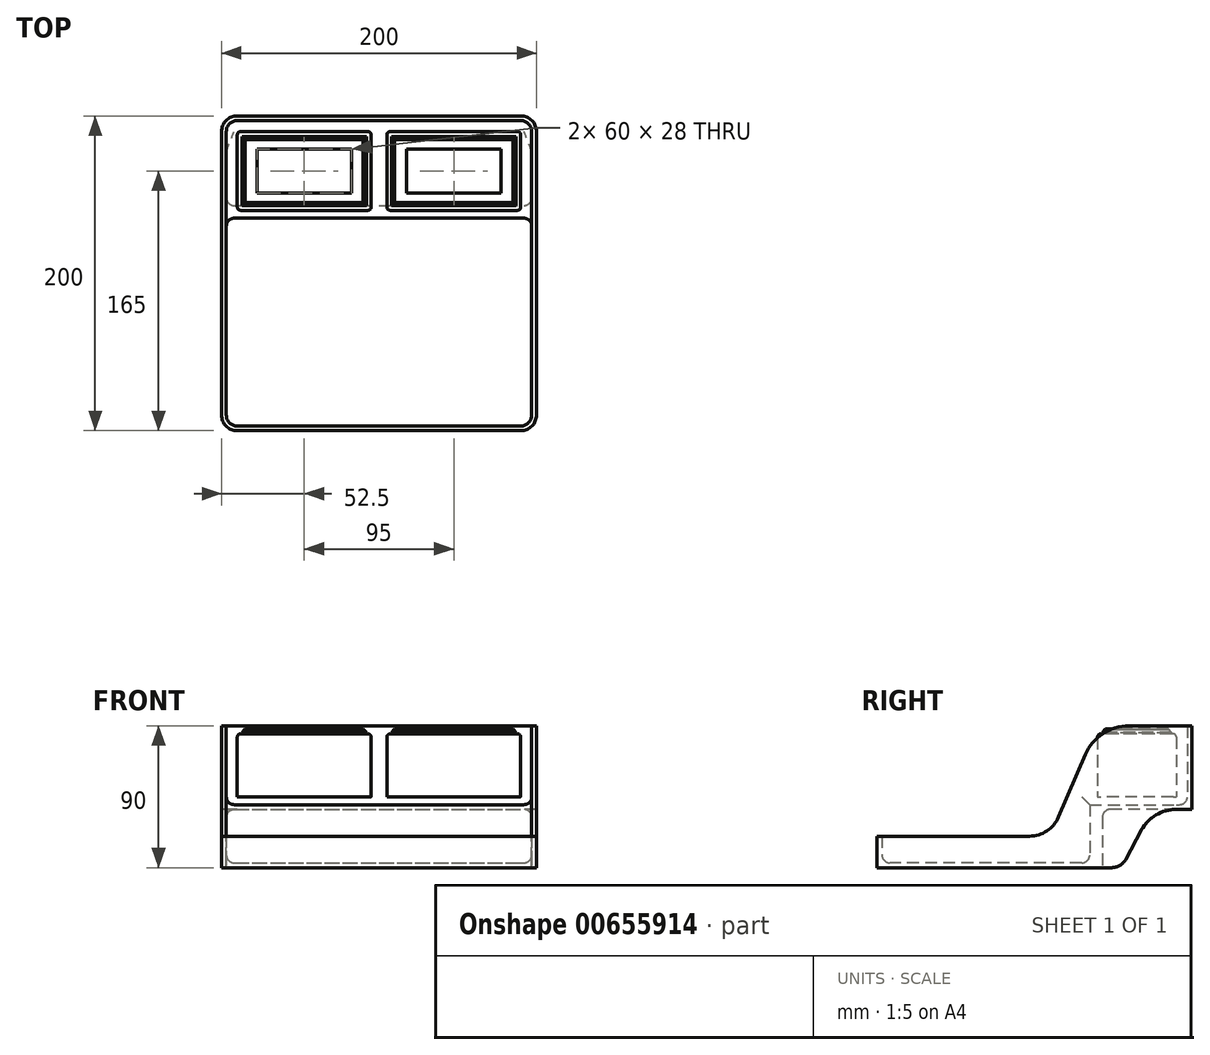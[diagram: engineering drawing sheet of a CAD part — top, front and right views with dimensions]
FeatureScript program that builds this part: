
annotation { "Feature Type Name" : "Feature", "Feature Type Description" : "" }
export const myFeature = defineFeature(function(context is Context, id is Id, definition is map)
    precondition{}
    {
        {
            var Q0;
            Q0=qCreatedBy(makeId("Top.planeOp"),FACE);
            var sketch = newSketch(context, id + "F0", { "sketchPlane" : qUnion([Q0])});
            skLineSegment(sketch, "E0.bottom", {"start": v(-90, 100) * mm, "end": v(90, 100) * mm});
            skLineSegment(sketch, "E0.top", {"start": v(-90, -100) * mm, "end": v(90, -100) * mm});
            skLineSegment(sketch, "E0.left", {"start": v(-100, 90) * mm, "end": v(-100, -90) * mm});
            skLineSegment(sketch, "E0.right", {"start": v(100, 90) * mm, "end": v(100, -90) * mm});
            skPoint(sketch, "E1.visualSharp", {"position": v(-100, 100) * mm});
            skArc(sketch, "E1.filletArc", {"start": v(-90, 100) * mm, "mid": v(-97.07, 97.07) * mm, "end": v(-100, 90) * mm});
            skPoint(sketch, "E2.visualSharp", {"position": v(100, 100) * mm});
            skArc(sketch, "E2.filletArc", {"start": v(100, 90) * mm, "mid": v(97.07, 97.07) * mm, "end": v(90, 100) * mm});
            skPoint(sketch, "E3.visualSharp", {"position": v(100, -100) * mm});
            skArc(sketch, "E3.filletArc", {"start": v(90, -100) * mm, "mid": v(97.07, -97.07) * mm, "end": v(100, -90) * mm});
            skPoint(sketch, "E4.visualSharp", {"position": v(-100, -100) * mm});
            skArc(sketch, "E4.filletArc", {"start": v(-100, -90) * mm, "mid": v(-97.07, -97.07) * mm, "end": v(-90, -100) * mm});
            skSolve(sketch);
        }
        {
            var Q0;
            Q0 = qSketchRegion(id + "F0", true);
            extrude(context, id + "F1", {"entities" : qUnion([Q0]), "depth" : 90 * mm, "offsetDistance" : 25 * mm});
        }
        {
            var Q0;
            Q0=qCreatedBy(makeId("Top.planeOp"),FACE);
            var sketch = newSketch(context, id + "F2", { "sketchPlane" : qUnion([Q0])});
            skLineSegment(sketch, "E5.bottom", {"start": v(-97, 35) * mm, "end": v(97, 35) * mm});
            skLineSegment(sketch, "E5.top", {"start": v(-90, -97) * mm, "end": v(90, -97) * mm});
            skLineSegment(sketch, "E5.left", {"start": v(-97, 35) * mm, "end": v(-97, -90) * mm});
            skLineSegment(sketch, "E5.right", {"start": v(97, 35) * mm, "end": v(97, -90) * mm});
            skPoint(sketch, "E6.visualSharp", {"position": v(97, -97) * mm});
            skArc(sketch, "E6.filletArc", {"start": v(90, -97) * mm, "mid": v(94.95, -94.95) * mm, "end": v(97, -90) * mm});
            skPoint(sketch, "E7.visualSharp", {"position": v(-97, -97) * mm});
            skArc(sketch, "E7.filletArc", {"start": v(-97, -90) * mm, "mid": v(-94.95, -94.95) * mm, "end": v(-90, -97) * mm});
            skSolve(sketch);
        }
        {
            var Q0;
            Q0 = qSketchRegion(id + "F2", true);
            extrude(context, id + "F3", {"entities" : qUnion([Q0]), "depth" : 80 * mm, "offsetDistance" : 25 * mm});
        }
        {
            var Q0;
            Q0=makeQuery(id+"F3.opExtrude","CAP_EDGE",EDGE,{"disambiguationData":[OSD([sQuery(id+"F2.wireOp",EDGE,"E5.left")])],"isStart":true});
            var Q1;
            Q1=makeQuery(id+"F3.opExtrude","CAP_EDGE",EDGE,{"disambiguationData":[OSD([sQuery(id+"F2.wireOp",EDGE,"E7.filletArc")])],"isStart":true});
            var Q2;
            Q2=makeQuery(id+"F3.opExtrude","CAP_EDGE",EDGE,{"disambiguationData":[OSD([sQuery(id+"F2.wireOp",EDGE,"E5.top")])],"isStart":true});
            var Q3;
            Q3=makeQuery(id+"F3.opExtrude","CAP_EDGE",EDGE,{"disambiguationData":[OSD([sQuery(id+"F2.wireOp",EDGE,"E6.filletArc")])],"isStart":true});
            var Q4;
            Q4=makeQuery(id+"F3.opExtrude","CAP_EDGE",EDGE,{"disambiguationData":[OSD([sQuery(id+"F2.wireOp",EDGE,"E5.right")])],"isStart":true});
            var Q5;
            Q5=makeQuery(id+"F3.opExtrude","CAP_EDGE",EDGE,{"disambiguationData":[OSD([sQuery(id+"F2.wireOp",EDGE,"E5.bottom")])],"isStart":true});
            var Q6;
            Q6=makeQuery(id+"F3.opExtrude","SWEPT_EDGE",EDGE,{"disambiguationData":[OSD([sQuery(id+"F2.wireOp",EDGE,"E5.bottom"),sQuery(id+"F2.wireOp",EDGE,"E5.left")])]});
            var Q7;
            Q7=makeQuery(id+"F3.opExtrude","SWEPT_EDGE",EDGE,{"disambiguationData":[OSD([sQuery(id+"F2.wireOp",EDGE,"E5.bottom"),sQuery(id+"F2.wireOp",EDGE,"E5.right")])]});
            fillet(context, id + "F4", {"entities" : qUnion([Q0, Q1, Q2, Q3, Q4, Q5, Q6, Q7]), "radius" : 5 * mm, "tangentPropagation" : true, "allowEdgeOverflow" : false});
        }
        {
            var Q0;
            Q0=makeQuery(id+"F3.opExtrude","SWEPT_BODY",BODY,{"disambiguationData":[OSD([sQuery(id+"F2.wireOp",EDGE,"E5.bottom"),sQuery(id+"F2.wireOp",EDGE,"E5.top"),sQuery(id+"F2.wireOp",EDGE,"E5.left"),sQuery(id+"F2.wireOp",EDGE,"E5.right"),sQuery(id+"F2.wireOp",EDGE,"E6.filletArc"),sQuery(id+"F2.wireOp",EDGE,"E7.filletArc")])]});
            var Q1;
            Q1=qCreatedBy(makeId("Top.planeOp"),FACE);
            transform(context, id + "F5", {"entities" : qUnion([Q0]), "transformType" : TransformType.TRANSLATION_DISTANCE, "transformDirection" : qUnion([Q1]), "distance" : 3 * mm, "makeCopy" : false});
        }
        {
            var Q0;
            Q0=qCreatedBy(makeId("Top.planeOp"),FACE);
            var sketch = newSketch(context, id + "F6", { "sketchPlane" : qUnion([Q0])});
            skLineSegment(sketch, "E8.bottom", {"start": v(-97, 30) * mm, "end": v(97, 30) * mm});
            skLineSegment(sketch, "E8.top", {"start": v(-90, 97) * mm, "end": v(90, 97) * mm});
            skLineSegment(sketch, "E8.left", {"start": v(-97, 30) * mm, "end": v(-97, 90) * mm});
            skLineSegment(sketch, "E8.right", {"start": v(97, 30) * mm, "end": v(97, 90) * mm});
            skPoint(sketch, "E9.visualSharp", {"position": v(-97, 97) * mm});
            skArc(sketch, "E9.filletArc", {"start": v(-90, 97) * mm, "mid": v(-94.95, 94.95) * mm, "end": v(-97, 90) * mm});
            skPoint(sketch, "E10.visualSharp", {"position": v(97, 97) * mm});
            skArc(sketch, "E10.filletArc", {"start": v(97, 90) * mm, "mid": v(94.95, 94.95) * mm, "end": v(90, 97) * mm});
            skSolve(sketch);
        }
        {
            var Q0;
            Q0 = qSketchRegion(id + "F6", true);
            extrude(context, id + "F7", {"entities" : qUnion([Q0]), "depth" : 50 * mm, "offsetDistance" : 25 * mm});
        }
        {
            var Q0;
            Q0=makeQuery(id+"F7.opExtrude","CAP_EDGE",EDGE,{"disambiguationData":[OSD([sQuery(id+"F6.wireOp",EDGE,"E8.left")])],"isStart":true});
            var Q1;
            Q1=makeQuery(id+"F7.opExtrude","CAP_EDGE",EDGE,{"disambiguationData":[OSD([sQuery(id+"F6.wireOp",EDGE,"E9.filletArc")])],"isStart":true});
            var Q2;
            Q2=makeQuery(id+"F7.opExtrude","CAP_EDGE",EDGE,{"disambiguationData":[OSD([sQuery(id+"F6.wireOp",EDGE,"E8.top")])],"isStart":true});
            var Q3;
            Q3=makeQuery(id+"F7.opExtrude","CAP_EDGE",EDGE,{"disambiguationData":[OSD([sQuery(id+"F6.wireOp",EDGE,"E10.filletArc")])],"isStart":true});
            var Q4;
            Q4=makeQuery(id+"F7.opExtrude","CAP_EDGE",EDGE,{"disambiguationData":[OSD([sQuery(id+"F6.wireOp",EDGE,"E8.right")])],"isStart":true});
            fillet(context, id + "F8", {"entities" : qUnion([Q0, Q1, Q2, Q3, Q4]), "radius" : 5 * mm, "tangentPropagation" : true, "allowEdgeOverflow" : false});
        }
        {
            var Q0;
            Q0=makeQuery(id+"F7.opExtrude","SWEPT_BODY",BODY,{"disambiguationData":[OSD([sQuery(id+"F6.wireOp",EDGE,"E8.bottom"),sQuery(id+"F6.wireOp",EDGE,"E8.top"),sQuery(id+"F6.wireOp",EDGE,"E8.left"),sQuery(id+"F6.wireOp",EDGE,"E8.right"),sQuery(id+"F6.wireOp",EDGE,"E9.filletArc"),sQuery(id+"F6.wireOp",EDGE,"E10.filletArc")])]});
            var Q1;
            Q1=qCreatedBy(makeId("Top.planeOp"),FACE);
            transform(context, id + "F9", {"entities" : qUnion([Q0]), "transformType" : TransformType.TRANSLATION_DISTANCE, "transformDirection" : qUnion([Q1]), "distance" : 40 * mm, "makeCopy" : false});
        }
        {
            var Q0;
            Q0=makeQuery(id+"F7.opExtrude","SWEPT_BODY",BODY,{"disambiguationData":[OSD([sQuery(id+"F6.wireOp",EDGE,"E8.bottom"),sQuery(id+"F6.wireOp",EDGE,"E8.top"),sQuery(id+"F6.wireOp",EDGE,"E8.left"),sQuery(id+"F6.wireOp",EDGE,"E8.right"),sQuery(id+"F6.wireOp",EDGE,"E9.filletArc"),sQuery(id+"F6.wireOp",EDGE,"E10.filletArc")])]});
            var Q1;
            Q1=makeQuery(id+"F3.opExtrude","SWEPT_BODY",BODY,{"disambiguationData":[OSD([sQuery(id+"F2.wireOp",EDGE,"E5.bottom"),sQuery(id+"F2.wireOp",EDGE,"E5.top"),sQuery(id+"F2.wireOp",EDGE,"E5.left"),sQuery(id+"F2.wireOp",EDGE,"E5.right"),sQuery(id+"F2.wireOp",EDGE,"E6.filletArc"),sQuery(id+"F2.wireOp",EDGE,"E7.filletArc")])]});
            var Q2;
            Q2=makeQuery(id+"F1.opExtrude","SWEPT_BODY",BODY,{"disambiguationData":[OSD([sQuery(id+"F0.wireOp",EDGE,"E0.bottom"),sQuery(id+"F0.wireOp",EDGE,"E0.top"),sQuery(id+"F0.wireOp",EDGE,"E0.left"),sQuery(id+"F0.wireOp",EDGE,"E0.right"),sQuery(id+"F0.wireOp",EDGE,"E1.filletArc"),sQuery(id+"F0.wireOp",EDGE,"E2.filletArc"),sQuery(id+"F0.wireOp",EDGE,"E3.filletArc"),sQuery(id+"F0.wireOp",EDGE,"E4.filletArc")])]});
            booleanBodies(context, id + "F10", {"operationType" : BooleanOperationType.SUBTRACTION, "tools" : qUnion([Q0, Q1]), "targets" : qUnion([Q2])});
        }
        {
            var Q0;
            Q0=qCreatedBy(makeId("Top.planeOp"),FACE);
            var sketch = newSketch(context, id + "F11", { "sketchPlane" : qUnion([Q0])});
            skLineSegment(sketch, "E11.bottom", {"start": v(-97, 105) * mm, "end": v(97, 105) * mm});
            skLineSegment(sketch, "E11.top", {"start": v(-92, 43) * mm, "end": v(92, 43) * mm});
            skLineSegment(sketch, "E11.left", {"start": v(-97, 105) * mm, "end": v(-97, 48) * mm});
            skLineSegment(sketch, "E11.right", {"start": v(97, 105) * mm, "end": v(97, 48) * mm});
            skPoint(sketch, "E12.visualSharp", {"position": v(-97, 43) * mm});
            skArc(sketch, "E12.filletArc", {"start": v(-97, 48) * mm, "mid": v(-95.54, 44.46) * mm, "end": v(-92, 43) * mm});
            skPoint(sketch, "E13.visualSharp", {"position": v(97, 43) * mm});
            skArc(sketch, "E13.filletArc", {"start": v(92, 43) * mm, "mid": v(95.54, 44.46) * mm, "end": v(97, 48) * mm});
            skSolve(sketch);
        }
        {
            var Q0;
            Q0=makeQuery(id+"F11.imprint","IMPRINT",FACE,{"disambiguationData":[TD([[makeQuery(id+"F11.imprint","IMPRINT",EDGE,{"derivedFrom":sQuery(id+"F11.wireOp",EDGE,"E11.bottom")}),-1.0]])]});
            extrude(context, id + "F12", {"entities" : qUnion([Q0]), "depth" : 37 * mm, "offsetDistance" : 25 * mm});
        }
        {
            var Q0;
            Q0=makeQuery(id+"F12.opExtrude","CAP_EDGE",EDGE,{"disambiguationData":[OSD([sQuery(id+"F11.wireOp",EDGE,"E11.top")])],"isStart":false});
            var Q1;
            Q1=makeQuery(id+"F12.opExtrude","CAP_EDGE",EDGE,{"disambiguationData":[OSD([sQuery(id+"F11.wireOp",EDGE,"E13.filletArc")])],"isStart":false});
            var Q2;
            Q2=makeQuery(id+"F12.opExtrude","CAP_EDGE",EDGE,{"disambiguationData":[OSD([sQuery(id+"F11.wireOp",EDGE,"E11.right")])],"isStart":false});
            var Q3;
            Q3=makeQuery(id+"F12.opExtrude","CAP_EDGE",EDGE,{"disambiguationData":[OSD([sQuery(id+"F11.wireOp",EDGE,"E12.filletArc")])],"isStart":false});
            var Q4;
            Q4=makeQuery(id+"F12.opExtrude","CAP_EDGE",EDGE,{"disambiguationData":[OSD([sQuery(id+"F11.wireOp",EDGE,"E11.left")])],"isStart":false});
            fillet(context, id + "F13", {"entities" : qUnion([Q0, Q1, Q2, Q3, Q4]), "radius" : 5 * mm, "tangentPropagation" : true, "allowEdgeOverflow" : false});
        }
        {
            var Q0;
            Q0=makeQuery(id+"F12.opExtrude","SWEPT_BODY",BODY,{"disambiguationData":[OSD([sQuery(id+"F11.wireOp",EDGE,"E11.bottom"),sQuery(id+"F11.wireOp",EDGE,"E11.top"),sQuery(id+"F11.wireOp",EDGE,"E11.left"),sQuery(id+"F11.wireOp",EDGE,"E11.right"),sQuery(id+"F11.wireOp",EDGE,"E12.filletArc"),sQuery(id+"F11.wireOp",EDGE,"E13.filletArc")])]});
            var Q1;
            Q1=makeQuery(id+"F1.opExtrude","SWEPT_BODY",BODY,{"disambiguationData":[OSD([sQuery(id+"F0.wireOp",EDGE,"E0.bottom"),sQuery(id+"F0.wireOp",EDGE,"E0.top"),sQuery(id+"F0.wireOp",EDGE,"E0.left"),sQuery(id+"F0.wireOp",EDGE,"E0.right"),sQuery(id+"F0.wireOp",EDGE,"E1.filletArc"),sQuery(id+"F0.wireOp",EDGE,"E2.filletArc"),sQuery(id+"F0.wireOp",EDGE,"E3.filletArc"),sQuery(id+"F0.wireOp",EDGE,"E4.filletArc")])]});
            booleanBodies(context, id + "F14", {"operationType" : BooleanOperationType.SUBTRACTION, "tools" : qUnion([Q0]), "targets" : qUnion([Q1])});
        }
        {
            var Q0;
            Q0=qCreatedBy(makeId("Right.planeOp"),FACE);
            var sketch = newSketch(context, id + "F15", { "sketchPlane" : qUnion([Q0])});
            skLineSegment(sketch, "E14", {"start": v(105, 37) * mm, "end": v(89.9, 37) * mm});
            skLineSegment(sketch, "E15", {"start": v(67.91, 23.89) * mm, "end": v(57.84, 5.24) * mm});
            skLineSegment(sketch, "E16", {"start": v(49.04, 0) * mm, "end": v(25.08, 0) * mm});
            skLineSegment(sketch, "E17", {"start": v(25.08, 0) * mm, "end": v(25.08, -10) * mm});
            skLineSegment(sketch, "E18", {"start": v(25.08, -10) * mm, "end": v(105, -10) * mm});
            skLineSegment(sketch, "E19", {"start": v(105, -10) * mm, "end": v(105, 37) * mm});
            skPoint(sketch, "E20.visualSharp", {"position": v(75, 37) * mm});
            skArc(sketch, "E20.filletArc", {"start": v(89.9, 37) * mm, "mid": v(77.1, 33.47) * mm, "end": v(67.91, 23.89) * mm});
            skPoint(sketch, "E21.visualSharp", {"position": v(55, 0) * mm});
            skArc(sketch, "E21.filletArc", {"start": v(49.04, 0) * mm, "mid": v(54.16, 1.41) * mm, "end": v(57.84, 5.24) * mm});
            skSolve(sketch);
        }
        {
            var Q0;
            Q0=makeQuery(id+"F15.imprint","IMPRINT",FACE,{"disambiguationData":[TD([[makeQuery(id+"F15.imprint","IMPRINT",EDGE,{"derivedFrom":sQuery(id+"F15.wireOp",EDGE,"E14")}),1.0]])]});
            extrude(context, id + "F16", {"entities" : qUnion([Q0]), "endBound" : BoundingType.SYMMETRIC, "depth" : 210 * mm, "offsetDistance" : 25 * mm});
        }
        {
            var Q0;
            Q0=qCreatedBy(makeId("Right.planeOp"),FACE);
            var sketch = newSketch(context, id + "F17", { "sketchPlane" : qUnion([Q0])});
            skLineSegment(sketch, "E22", {"start": v(-105, 20) * mm, "end": v(-3.19, 20) * mm});
            skLineSegment(sketch, "E23", {"start": v(15.2, 32.12) * mm, "end": v(32.2, 71.82) * mm});
            skLineSegment(sketch, "E24", {"start": v(59.78, 90) * mm, "end": v(80, 90) * mm});
            skLineSegment(sketch, "E25", {"start": v(80, 90) * mm, "end": v(80, 100) * mm});
            skLineSegment(sketch, "E26", {"start": v(80, 100) * mm, "end": v(-105, 100) * mm});
            skLineSegment(sketch, "E27", {"start": v(-105, 100) * mm, "end": v(-105, 20) * mm});
            skPoint(sketch, "E28.visualSharp", {"position": v(40, 90) * mm});
            skArc(sketch, "E28.filletArc", {"start": v(59.78, 90) * mm, "mid": v(43.27, 85.05) * mm, "end": v(32.2, 71.82) * mm});
            skPoint(sketch, "E29.visualSharp", {"position": v(10, 20) * mm});
            skArc(sketch, "E29.filletArc", {"start": v(-3.19, 20) * mm, "mid": v(7.82, 23.3) * mm, "end": v(15.2, 32.12) * mm});
            skSolve(sketch);
        }
        {
            var Q0;
            Q0=makeQuery(id+"F17.imprint","IMPRINT",FACE,{"disambiguationData":[TD([[makeQuery(id+"F17.imprint","IMPRINT",EDGE,{"derivedFrom":sQuery(id+"F17.wireOp",EDGE,"E22")}),1.0]])]});
            extrude(context, id + "F18", {"entities" : qUnion([Q0]), "endBound" : BoundingType.SYMMETRIC, "depth" : 210 * mm, "offsetDistance" : 25 * mm});
        }
        {
            var Q0;
            Q0=makeQuery(id+"F16.opExtrude","SWEPT_BODY",BODY,{"disambiguationData":[OSD([sQuery(id+"F15.wireOp",EDGE,"E14"),sQuery(id+"F15.wireOp",EDGE,"E15"),sQuery(id+"F15.wireOp",EDGE,"E16"),sQuery(id+"F15.wireOp",EDGE,"E17"),sQuery(id+"F15.wireOp",EDGE,"E18"),sQuery(id+"F15.wireOp",EDGE,"E19"),sQuery(id+"F15.wireOp",EDGE,"E20.filletArc"),sQuery(id+"F15.wireOp",EDGE,"E21.filletArc")])]});
            var Q1;
            Q1=makeQuery(id+"F18.opExtrude","SWEPT_BODY",BODY,{"disambiguationData":[OSD([sQuery(id+"F17.wireOp",EDGE,"E22"),sQuery(id+"F17.wireOp",EDGE,"E23"),sQuery(id+"F17.wireOp",EDGE,"E24"),sQuery(id+"F17.wireOp",EDGE,"E25"),sQuery(id+"F17.wireOp",EDGE,"E26"),sQuery(id+"F17.wireOp",EDGE,"E27"),sQuery(id+"F17.wireOp",EDGE,"E28.filletArc"),sQuery(id+"F17.wireOp",EDGE,"E29.filletArc")])]});
            var Q2;
            Q2=makeQuery(id+"F1.opExtrude","SWEPT_BODY",BODY,{"disambiguationData":[OSD([sQuery(id+"F0.wireOp",EDGE,"E0.bottom"),sQuery(id+"F0.wireOp",EDGE,"E0.top"),sQuery(id+"F0.wireOp",EDGE,"E0.left"),sQuery(id+"F0.wireOp",EDGE,"E0.right"),sQuery(id+"F0.wireOp",EDGE,"E1.filletArc"),sQuery(id+"F0.wireOp",EDGE,"E2.filletArc"),sQuery(id+"F0.wireOp",EDGE,"E3.filletArc"),sQuery(id+"F0.wireOp",EDGE,"E4.filletArc")])]});
            booleanBodies(context, id + "F19", {"operationType" : BooleanOperationType.SUBTRACTION, "tools" : qUnion([Q0, Q1]), "targets" : qUnion([Q2])});
        }
        {
            var Q0;
            Q0=qCreatedBy(makeId("Top.planeOp"),FACE);
            var sketch = newSketch(context, id + "F20", { "sketchPlane" : qUnion([Q0])});
            skLineSegment(sketch, "E30.bottom", {"start": v(5, 90) * mm, "end": v(90, 90) * mm});
            skLineSegment(sketch, "E30.top", {"start": v(5, 40) * mm, "end": v(90, 40) * mm});
            skLineSegment(sketch, "E30.left", {"start": v(5, 90) * mm, "end": v(5, 40) * mm});
            skLineSegment(sketch, "E30.right", {"start": v(90, 90) * mm, "end": v(90, 40) * mm});
            skLineSegment(sketch, "E31.bottom", {"start": v(-5, 90) * mm, "end": v(-90, 90) * mm});
            skLineSegment(sketch, "E31.top", {"start": v(-5, 40) * mm, "end": v(-90, 40) * mm});
            skLineSegment(sketch, "E31.left", {"start": v(-5, 90) * mm, "end": v(-5, 40) * mm});
            skLineSegment(sketch, "E31.right", {"start": v(-90, 90) * mm, "end": v(-90, 40) * mm});
            skSolve(sketch);
        }
        {
            var Q0;
            Q0=makeQuery(id+"F20.imprint","IMPRINT",FACE,{"disambiguationData":[TD([[makeQuery(id+"F20.imprint","IMPRINT",EDGE,{"derivedFrom":sQuery(id+"F20.wireOp",EDGE,"E31.bottom")}),1.0]])]});
            var Q1;
            Q1=makeQuery(id+"F20.imprint","IMPRINT",FACE,{"disambiguationData":[TD([[makeQuery(id+"F20.imprint","IMPRINT",EDGE,{"derivedFrom":sQuery(id+"F20.wireOp",EDGE,"E30.bottom")}),-1.0]])]});
            extrude(context, id + "F21", {"entities" : qUnion([Q0, Q1]), "depth" : 40 * mm, "offsetDistance" : 25 * mm});
        }
        {
            var Q0;
            Q0=makeQuery(id+"F21.opExtrude","SWEPT_EDGE",EDGE,{"disambiguationData":[OSD([sQuery(id+"F20.wireOp",EDGE,"E31.top"),sQuery(id+"F20.wireOp",EDGE,"E31.right")])]});
            var Q1;
            Q1=makeQuery(id+"F21.opExtrude","SWEPT_EDGE",EDGE,{"disambiguationData":[OSD([sQuery(id+"F20.wireOp",EDGE,"E31.top"),sQuery(id+"F20.wireOp",EDGE,"E31.left")])]});
            var Q2;
            Q2=makeQuery(id+"F21.opExtrude","SWEPT_EDGE",EDGE,{"disambiguationData":[OSD([sQuery(id+"F20.wireOp",EDGE,"E30.top"),sQuery(id+"F20.wireOp",EDGE,"E30.left")])]});
            var Q3;
            Q3=makeQuery(id+"F21.opExtrude","SWEPT_EDGE",EDGE,{"disambiguationData":[OSD([sQuery(id+"F20.wireOp",EDGE,"E30.top"),sQuery(id+"F20.wireOp",EDGE,"E30.right")])]});
            var Q4;
            Q4=makeQuery(id+"F21.opExtrude","SWEPT_EDGE",EDGE,{"disambiguationData":[OSD([sQuery(id+"F20.wireOp",EDGE,"E31.bottom"),sQuery(id+"F20.wireOp",EDGE,"E31.right")])]});
            var Q5;
            Q5=makeQuery(id+"F21.opExtrude","SWEPT_EDGE",EDGE,{"disambiguationData":[OSD([sQuery(id+"F20.wireOp",EDGE,"E31.bottom"),sQuery(id+"F20.wireOp",EDGE,"E31.left")])]});
            var Q6;
            Q6=makeQuery(id+"F21.opExtrude","SWEPT_EDGE",EDGE,{"disambiguationData":[OSD([sQuery(id+"F20.wireOp",EDGE,"E30.bottom"),sQuery(id+"F20.wireOp",EDGE,"E30.left")])]});
            var Q7;
            Q7=makeQuery(id+"F21.opExtrude","SWEPT_EDGE",EDGE,{"disambiguationData":[OSD([sQuery(id+"F20.wireOp",EDGE,"E30.bottom"),sQuery(id+"F20.wireOp",EDGE,"E30.right")])]});
            var Q8;
            Q8=makeQuery(id+"F21.opExtrude","CAP_EDGE",EDGE,{"disambiguationData":[OSD([sQuery(id+"F20.wireOp",EDGE,"E31.bottom")])],"isStart":false});
            var Q9;
            Q9=makeQuery(id+"F21.opExtrude","CAP_EDGE",EDGE,{"disambiguationData":[OSD([sQuery(id+"F20.wireOp",EDGE,"E31.right")])],"isStart":false});
            var Q10;
            Q10=makeQuery(id+"F21.opExtrude","CAP_EDGE",EDGE,{"disambiguationData":[OSD([sQuery(id+"F20.wireOp",EDGE,"E31.left")])],"isStart":false});
            var Q11;
            Q11=makeQuery(id+"F21.opExtrude","CAP_EDGE",EDGE,{"disambiguationData":[OSD([sQuery(id+"F20.wireOp",EDGE,"E30.left")])],"isStart":false});
            var Q12;
            Q12=makeQuery(id+"F21.opExtrude","CAP_EDGE",EDGE,{"disambiguationData":[OSD([sQuery(id+"F20.wireOp",EDGE,"E30.right")])],"isStart":false});
            var Q13;
            Q13=makeQuery(id+"F21.opExtrude","CAP_EDGE",EDGE,{"disambiguationData":[OSD([sQuery(id+"F20.wireOp",EDGE,"E30.top")])],"isStart":false});
            var Q14;
            Q14=makeQuery(id+"F21.opExtrude","CAP_EDGE",EDGE,{"disambiguationData":[OSD([sQuery(id+"F20.wireOp",EDGE,"E30.bottom")])],"isStart":false});
            var Q15;
            Q15=makeQuery(id+"F21.opExtrude","CAP_EDGE",EDGE,{"disambiguationData":[OSD([sQuery(id+"F20.wireOp",EDGE,"E31.top")])],"isStart":false});
            fillet(context, id + "F22", {"entities" : qUnion([Q0, Q1, Q2, Q3, Q4, Q5, Q6, Q7, Q8, Q9, Q10, Q11, Q12, Q13, Q14, Q15]), "radius" : 2 * mm, "tangentPropagation" : true, "allowEdgeOverflow" : false});
        }
        {
            var Q0;
            Q0=makeQuery(id+"F21.opExtrude","SWEPT_BODY",BODY,{"disambiguationData":[OSD([sQuery(id+"F20.wireOp",EDGE,"E31.bottom"),sQuery(id+"F20.wireOp",EDGE,"E31.top"),sQuery(id+"F20.wireOp",EDGE,"E31.left"),sQuery(id+"F20.wireOp",EDGE,"E31.right")])]});
            var Q1;
            Q1=makeQuery(id+"F21.opExtrude","SWEPT_BODY",BODY,{"disambiguationData":[OSD([sQuery(id+"F20.wireOp",EDGE,"E30.bottom"),sQuery(id+"F20.wireOp",EDGE,"E30.top"),sQuery(id+"F20.wireOp",EDGE,"E30.left"),sQuery(id+"F20.wireOp",EDGE,"E30.right")])]});
            var Q2;
            Q2=qCreatedBy(makeId("Top.planeOp"),FACE);
            transform(context, id + "F23", {"entities" : qUnion([Q0, Q1]), "transformType" : TransformType.TRANSLATION_DISTANCE, "transformDirection" : qUnion([Q2]), "distance" : 45 * mm, "makeCopy" : false});
        }
        {
            var Q0;
            Q0=qCreatedBy(makeId("Top.planeOp"),FACE);
            var sketch = newSketch(context, id + "F24", { "sketchPlane" : qUnion([Q0])});
            skLineSegment(sketch, "E32.bottom", {"start": v(8, 87) * mm, "end": v(87, 87) * mm});
            skLineSegment(sketch, "E32.top", {"start": v(8, 43) * mm, "end": v(87, 43) * mm});
            skLineSegment(sketch, "E32.left", {"start": v(8, 87) * mm, "end": v(8, 43) * mm});
            skLineSegment(sketch, "E32.right", {"start": v(87, 87) * mm, "end": v(87, 43) * mm});
            skLineSegment(sketch, "E33.bottom", {"start": v(-87, 87) * mm, "end": v(-8, 87) * mm});
            skLineSegment(sketch, "E33.top", {"start": v(-87, 43) * mm, "end": v(-8, 43) * mm});
            skLineSegment(sketch, "E33.left", {"start": v(-87, 87) * mm, "end": v(-87, 43) * mm});
            skLineSegment(sketch, "E33.right", {"start": v(-8, 87) * mm, "end": v(-8, 43) * mm});
            skSolve(sketch);
        }
        {
            var Q0;
            Q0 = qSketchRegion(id + "F24", true);
            extrude(context, id + "F25", {"entities" : qUnion([Q0]), "depth" : 3 * mm, "offsetDistance" : 25 * mm});
        }
        {
            var Q0;
            Q0=makeQuery(id+"F25.opExtrude","CAP_EDGE",EDGE,{"disambiguationData":[OSD([sQuery(id+"F24.wireOp",EDGE,"E33.left")])],"isStart":false});
            var Q1;
            Q1=makeQuery(id+"F25.opExtrude","CAP_EDGE",EDGE,{"disambiguationData":[OSD([sQuery(id+"F24.wireOp",EDGE,"E33.top")])],"isStart":false});
            var Q2;
            Q2=makeQuery(id+"F25.opExtrude","CAP_EDGE",EDGE,{"disambiguationData":[OSD([sQuery(id+"F24.wireOp",EDGE,"E33.right")])],"isStart":false});
            var Q3;
            Q3=makeQuery(id+"F25.opExtrude","CAP_EDGE",EDGE,{"disambiguationData":[OSD([sQuery(id+"F24.wireOp",EDGE,"E33.bottom")])],"isStart":false});
            var Q4;
            Q4=makeQuery(id+"F25.opExtrude","CAP_EDGE",EDGE,{"disambiguationData":[OSD([sQuery(id+"F24.wireOp",EDGE,"E32.left")])],"isStart":false});
            var Q5;
            Q5=makeQuery(id+"F25.opExtrude","CAP_EDGE",EDGE,{"disambiguationData":[OSD([sQuery(id+"F24.wireOp",EDGE,"E32.bottom")])],"isStart":false});
            var Q6;
            Q6=makeQuery(id+"F25.opExtrude","CAP_EDGE",EDGE,{"disambiguationData":[OSD([sQuery(id+"F24.wireOp",EDGE,"E32.top")])],"isStart":false});
            var Q7;
            Q7=makeQuery(id+"F25.opExtrude","CAP_EDGE",EDGE,{"disambiguationData":[OSD([sQuery(id+"F24.wireOp",EDGE,"E32.right")])],"isStart":false});
            chamfer(context, id + "F26", {"entities" : qUnion([Q0, Q1, Q2, Q3, Q4, Q5, Q6, Q7]), "width" : 2 * mm, "tangentPropagation" : true});
        }
        {
            var Q0;
            Q0=makeQuery(id+"F25.opExtrude","SWEPT_BODY",BODY,{"disambiguationData":[OSD([sQuery(id+"F24.wireOp",EDGE,"E33.bottom"),sQuery(id+"F24.wireOp",EDGE,"E33.top"),sQuery(id+"F24.wireOp",EDGE,"E33.left"),sQuery(id+"F24.wireOp",EDGE,"E33.right")])]});
            var Q1;
            Q1=makeQuery(id+"F25.opExtrude","SWEPT_BODY",BODY,{"disambiguationData":[OSD([sQuery(id+"F24.wireOp",EDGE,"E32.bottom"),sQuery(id+"F24.wireOp",EDGE,"E32.top"),sQuery(id+"F24.wireOp",EDGE,"E32.left"),sQuery(id+"F24.wireOp",EDGE,"E32.right")])]});
            var Q2;
            Q2=qCreatedBy(makeId("Top.planeOp"),FACE);
            transform(context, id + "F27", {"entities" : qUnion([Q0, Q1]), "transformType" : TransformType.TRANSLATION_DISTANCE, "transformDirection" : qUnion([Q2]), "distance" : 85 * mm, "makeCopy" : false});
        }
        {
            var Q0;
            Q0=makeQuery(id+"F24.imprint","IMPRINT",FACE,{"disambiguationData":[TD([[makeQuery(id+"F24.imprint","IMPRINT",EDGE,{"derivedFrom":sQuery(id+"F24.wireOp",EDGE,"E33.bottom")}),-1.0]])]});
            var sketch = newSketch(context, id + "F28", { "sketchPlane" : qUnion([Q0])});
            skLineSegment(sketch, "E34.bottom", {"start": v(10, 85) * mm, "end": v(85, 85) * mm});
            skLineSegment(sketch, "E34.top", {"start": v(10, 45) * mm, "end": v(85, 45) * mm});
            skLineSegment(sketch, "E34.left", {"start": v(10, 85) * mm, "end": v(10, 45) * mm});
            skLineSegment(sketch, "E34.right", {"start": v(85, 85) * mm, "end": v(85, 45) * mm});
            skLineSegment(sketch, "E35.bottom", {"start": v(-85, 85) * mm, "end": v(-10, 85) * mm});
            skLineSegment(sketch, "E35.top", {"start": v(-85, 45) * mm, "end": v(-10, 45) * mm});
            skLineSegment(sketch, "E35.left", {"start": v(-85, 85) * mm, "end": v(-85, 45) * mm});
            skLineSegment(sketch, "E35.right", {"start": v(-10, 85) * mm, "end": v(-10, 45) * mm});
            skSolve(sketch);
        }
        {
            var Q0;
            Q0 = qSketchRegion(id + "F28", true);
            extrude(context, id + "F29", {"entities" : qUnion([Q0]), "depth" : 0.5 * mm, "offsetDistance" : 25 * mm});
        }
        {
            var Q0;
            Q0=makeQuery(id+"F24.imprint","IMPRINT",FACE,{"disambiguationData":[TD([[makeQuery(id+"F24.imprint","IMPRINT",EDGE,{"derivedFrom":sQuery(id+"F24.wireOp",EDGE,"E33.bottom")}),-1.0]])]});
            var sketch = newSketch(context, id + "F30", { "sketchPlane" : qUnion([Q0])});
            skLineSegment(sketch, "E36.bottom", {"start": v(-77.5, 79) * mm, "end": v(-17.5, 79) * mm});
            skLineSegment(sketch, "E36.top", {"start": v(-77.5, 51) * mm, "end": v(-17.5, 51) * mm});
            skLineSegment(sketch, "E36.left", {"start": v(-77.5, 79) * mm, "end": v(-77.5, 51) * mm});
            skLineSegment(sketch, "E36.right", {"start": v(-17.5, 79) * mm, "end": v(-17.5, 51) * mm});
            skLineSegment(sketch, "E37.bottom", {"start": v(17.5, 79) * mm, "end": v(77.5, 79) * mm});
            skLineSegment(sketch, "E37.top", {"start": v(17.5, 51) * mm, "end": v(77.5, 51) * mm});
            skLineSegment(sketch, "E37.left", {"start": v(17.5, 79) * mm, "end": v(17.5, 51) * mm});
            skLineSegment(sketch, "E37.right", {"start": v(77.5, 79) * mm, "end": v(77.5, 51) * mm});
            skSolve(sketch);
        }
        {
            var Q0;
            Q0 = qSketchRegion(id + "F30", true);
            extrude(context, id + "F31", {"entities" : qUnion([Q0]), "depth" : 1 * mm, "offsetDistance" : 25 * mm});
        }
        {
            var Q0;
            Q0=makeQuery(id+"F31.opExtrude","SWEPT_BODY",BODY,{"disambiguationData":[OSD([sQuery(id+"F30.wireOp",EDGE,"E36.bottom"),sQuery(id+"F30.wireOp",EDGE,"E36.top"),sQuery(id+"F30.wireOp",EDGE,"E36.left"),sQuery(id+"F30.wireOp",EDGE,"E36.right")])]});
            var Q1;
            Q1=makeQuery(id+"F31.opExtrude","SWEPT_BODY",BODY,{"disambiguationData":[OSD([sQuery(id+"F30.wireOp",EDGE,"E37.bottom"),sQuery(id+"F30.wireOp",EDGE,"E37.top"),sQuery(id+"F30.wireOp",EDGE,"E37.left"),sQuery(id+"F30.wireOp",EDGE,"E37.right")])]});
            var Q2;
            Q2=makeQuery(id+"F29.opExtrude","SWEPT_BODY",BODY,{"disambiguationData":[OSD([sQuery(id+"F28.wireOp",EDGE,"E35.bottom"),sQuery(id+"F28.wireOp",EDGE,"E35.top"),sQuery(id+"F28.wireOp",EDGE,"E35.left"),sQuery(id+"F28.wireOp",EDGE,"E35.right")])]});
            var Q3;
            Q3=makeQuery(id+"F29.opExtrude","SWEPT_BODY",BODY,{"disambiguationData":[OSD([sQuery(id+"F28.wireOp",EDGE,"E34.bottom"),sQuery(id+"F28.wireOp",EDGE,"E34.top"),sQuery(id+"F28.wireOp",EDGE,"E34.left"),sQuery(id+"F28.wireOp",EDGE,"E34.right")])]});
            booleanBodies(context, id + "F32", {"operationType" : BooleanOperationType.SUBTRACTION, "tools" : qUnion([Q0, Q1]), "targets" : qUnion([Q2, Q3])});
        }
        {
            var Q0;
            Q0=makeQuery(id+"F29.opExtrude","SWEPT_BODY",BODY,{"disambiguationData":[OSD([sQuery(id+"F28.wireOp",EDGE,"E35.bottom"),sQuery(id+"F28.wireOp",EDGE,"E35.top"),sQuery(id+"F28.wireOp",EDGE,"E35.left"),sQuery(id+"F28.wireOp",EDGE,"E35.right")])]});
            var Q1;
            Q1=makeQuery(id+"F29.opExtrude","SWEPT_BODY",BODY,{"disambiguationData":[OSD([sQuery(id+"F28.wireOp",EDGE,"E34.bottom"),sQuery(id+"F28.wireOp",EDGE,"E34.top"),sQuery(id+"F28.wireOp",EDGE,"E34.left"),sQuery(id+"F28.wireOp",EDGE,"E34.right")])]});
            var Q2;
            Q2=qCreatedBy(makeId("Top.planeOp"),FACE);
            transform(context, id + "F33", {"entities" : qUnion([Q0, Q1]), "transformType" : TransformType.TRANSLATION_DISTANCE, "transformDirection" : qUnion([Q2]), "distance" : 87.6 * mm, "makeCopy" : false});
        }
    });
